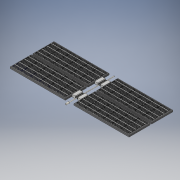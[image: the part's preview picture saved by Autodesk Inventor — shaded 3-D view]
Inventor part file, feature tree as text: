
AUTODESK INVENTOR PART (.ipt)
format: ipt  version: 2018 (Build 220112000, 112)  size: 5,240,832 bytes
history: native  units: in
note: dims shown in document units (in); Inventor stores cm internally (conversion verified against a paired STEP export)
features: other x6, sketch x5
ambient origin geometry x8: Origin, YZ Plane, XZ Plane, XY Plane, X Axis, Y Axis, Z Axis, Center Point
bodies: Solid1 (feature_tree), Solid2 (feature_tree), Solid3 (feature_tree), Solid4 (feature_tree), Solid5 (feature_tree)
feature tree (11):
  other  "Assembly_panel.iam"
  other  "Rod.ipt:1"
  other  "Solar_panel1.ipt:1"
  other  "Solar_panel1.ipt:3"
  other  "Solar_panel1_MIR.ipt:1"
  other  "Solar_panel1_MIR.ipt:2"
  sketch  "Sketch 1"  dims[d0=0.3937in]
  sketch  "Sketch7"
  sketch  "Sketch7_1"
  sketch  "Sketch7_2"
  sketch  "Sketch7_3"
